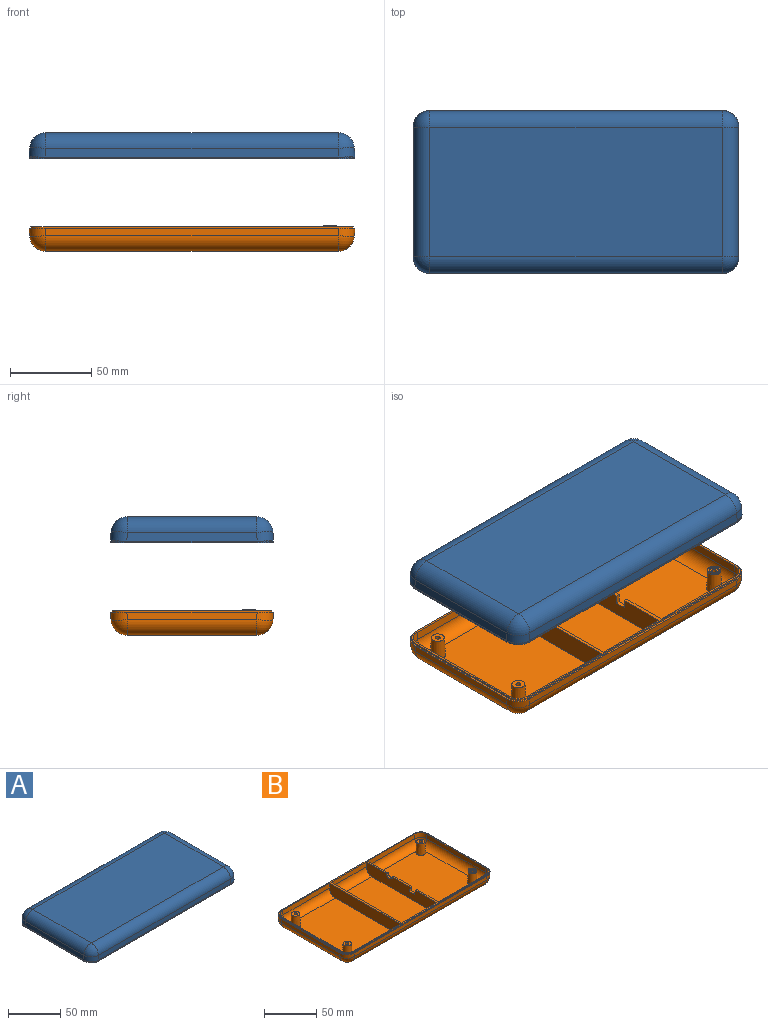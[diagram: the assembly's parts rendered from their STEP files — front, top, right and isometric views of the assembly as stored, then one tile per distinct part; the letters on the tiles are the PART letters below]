
ASSEMBLY  parts=2 mates=1
PART A: 92 faces, bbox 200.3x100.3x16.3 mm
  f0: plane 79.45x46.64mm, normal (0,0,-1), area 3705.3mm2, adj f3,f4,f28,f31
  f1: plane 48x5.42mm, normal (0,1,-0.05), area 258.9mm2, adj f4,f10,f28,f31
  f2: plane 48x5.42mm, normal (0,-1,-0.05), area 258.9mm2, adj f3,f10,f28,f31
  f3: cylinder r=8mm len=47.43mm, axis (-1,0,0), area 571.4mm2, adj f0,f2,f28,f31
  f4: cylinder r=8mm len=47.43mm, axis (-1,0,0), area 571.4mm2, adj f0,f1,f28,f31
  f5: plane 79.45x63.04mm, normal (0,0,-1), area 4871mm2, adj f8,f9,f14,f30,f32,f33
  f6: plane 64.01x5.42mm, normal (0,1,-0.05), area 345.8mm2, adj f9,f10,f22,f30
  f7: plane 64.01x5.42mm, normal (0,-1,-0.05), area 345.8mm2, adj f8,f10,f21,f30
  f8: cylinder r=8mm len=63.44mm, axis (-1,0,0), area 768.2mm2, adj f5,f7,f17,f30
  f9: cylinder r=8mm len=63.44mm, axis (-1,0,0), area 768.2mm2, adj f5,f6,f16,f30
  f10: plane 198.34x98.34mm, normal (0,0,-1), area 957.4mm2, adj f1,f2,f6,f7,f20,f21,f22,f23
  f11: plane 79.45x63.04mm, normal (0,0,-1), area 4871mm2, adj f12,f13,f15,f29,f35,f37
  f12: cylinder r=8mm len=79.45mm, axis (0,1,0), area 965.1mm2, adj f11,f18,f19,f27
  f13: cylinder r=8mm len=63.44mm, axis (-1,0,0), area 768.2mm2, adj f11,f18,f26,f29
  f14: cylinder r=8mm len=79.45mm, axis (0,1,0), area 965.1mm2, adj f5,f16,f17,f25
  f15: cylinder r=8mm len=63.44mm, axis (-1,0,0), area 768.2mm2, adj f11,f19,f24,f29
  f16: sphere r=8mm, area 95.3mm2, adj f9,f14,f22
  f17: sphere r=8mm, area 95.3mm2, adj f8,f14,f21
  f18: sphere r=8mm, area 95.3mm2, adj f12,f13,f20
  f19: sphere r=8mm, area 95.3mm2, adj f12,f15,f23
  f20: cylinder r=8mm len=8.27mm, axis (-0.05,0.05,-1), area 68.2mm2, adj f10,f18,f26,f27
  f21: cylinder r=8mm len=8.27mm, axis (0.05,0.05,-1), area 68.2mm2, adj f7,f10,f17,f25
  f22: cylinder r=8mm len=8.27mm, axis (0.05,-0.05,-1), area 68.2mm2, adj f6,f10,f16,f25
  f23: cylinder r=8mm len=8.27mm, axis (-0.05,-0.05,-1), area 68.2mm2, adj f10,f19,f24,f27
  f24: plane 64.01x5.42mm, normal (0,1,-0.05), area 345.8mm2, adj f10,f15,f23,f29
  f25: plane 80.02x5.42mm, normal (-1,0,-0.05), area 432.6mm2, adj f10,f14,f21,f22
  f26: plane 64.01x5.42mm, normal (0,-1,-0.05), area 345.8mm2, adj f10,f13,f20,f29
  f27: plane 80.02x5.42mm, normal (1,0,-0.05), area 432.6mm2, adj f10,f12,f20,f23
  f28: plane 96.16x13.17mm, normal (1,0,-0.05), area 1216.5mm2, adj f0,f1,f2,f3,f4,f10
  f29: plane 96.16x13.17mm, normal (-1,0,-0.05), area 1216.5mm2, adj f10,f11,f13,f15,f24,f26
  f30: plane 96.16x13.17mm, normal (1,0,-0.05), area 1216.5mm2, adj f5,f6,f7,f8,f9,f10
  f31: plane 96.16x13.17mm, normal (-1,0,-0.05), area 1216.5mm2, adj f0,f1,f2,f3,f4,f10
  f32: cone r=4mm half-angle=3deg, axis (0,0,1), area 329.7mm2, adj f5,f87
  f33: cone r=4mm half-angle=3deg, axis (0,0,1), area 355mm2, adj f5,f34
  f34: plane 8x8mm, normal (0,0,-1), area 47.1mm2, adj f33,f86
  f35: cone r=4mm half-angle=3deg, axis (0,0,1), area 355mm2, adj f11,f36
  f36: plane 8x8mm, normal (0,0,-1), area 47.1mm2, adj f35,f84
  f37: cone r=4mm half-angle=3deg, axis (0,0,1), area 355mm2, adj f11,f38
  f38: plane 8x8mm, normal (0,0,-1), area 47.1mm2, adj f37,f82
  f39: plane 199.99x99.99mm, normal (0,0,-1), area 579.7mm2, adj f40,f41,f42,f43,f44,f45,f46,f47
  f40: plane 180.02x1mm, normal (0,-1,0), area 180mm2, adj f10,f39,f41,f47
  f41: extruded ~8.99x8.99mm, area 14.1mm2, adj f10,f39,f40,f42
  f42: plane 80.02x1mm, normal (1,0,0), area 80mm2, adj f10,f39,f41,f43
  f43: extruded ~8.99x8.99mm, area 14.1mm2, adj f10,f39,f42,f44
  f44: plane 180.02x1mm, normal (0,1,0), area 180mm2, adj f10,f39,f43,f45
  f45: extruded ~8.99x8.99mm, area 14.1mm2, adj f10,f39,f44,f46
  f46: plane 80.02x1mm, normal (-1,0,0), area 80mm2, adj f10,f39,f45,f47
  f47: extruded ~8.99x8.99mm, area 14.1mm2, adj f10,f39,f40,f46
  f48: plane 180.02x1mm, normal (0,1,0), area 180mm2, adj f39,f49,f55,f76
  f49: extruded ~9.99x9.99mm, area 15.7mm2, adj f39,f48,f50,f77
  f50: plane 80.02x1mm, normal (-1,0,0), area 80mm2, adj f39,f49,f51,f78
  f51: extruded ~9.99x9.99mm, area 15.7mm2, adj f39,f50,f52,f79
  f52: plane 180.02x1mm, normal (0,-1,0), area 180mm2, adj f39,f51,f53,f80
  f53: extruded ~9.99x9.99mm, area 15.7mm2, adj f39,f52,f54,f73
  f54: plane 80.02x1mm, normal (1,0,0), area 80mm2, adj f39,f53,f55,f74
  f55: extruded ~9.99x9.99mm, area 15.7mm2, adj f39,f48,f54,f75
  f56: plane 179.45x79.45mm, normal (0,0,1), area 14256.9mm2, adj f57,f59,f61,f63
  f57: cylinder r=10mm len=179.45mm, axis (-1,0,0), area 2724.8mm2, adj f56,f58,f64,f65
  f58: sphere r=10mm, area 148.9mm2, adj f57,f59,f66
  f59: cylinder r=10mm len=79.45mm, axis (0,1,0), area 1206.4mm2, adj f56,f58,f60,f67
  f60: sphere r=10mm, area 148.9mm2, adj f59,f61,f68
  f61: cylinder r=10mm len=179.45mm, axis (-1,0,0), area 2724.8mm2, adj f56,f60,f62,f69
  f62: sphere r=10mm, area 148.9mm2, adj f61,f63,f70
  f63: cylinder r=10mm len=79.45mm, axis (0,1,0), area 1206.4mm2, adj f56,f62,f64,f71
  f64: sphere r=10mm, area 148.9mm2, adj f57,f63,f72
  f65: plane 180.02x5.42mm, normal (0,-1,0.05), area 975.3mm2, adj f57,f66,f72,f80
  f66: cylinder r=10mm len=10.27mm, axis (-0.05,-0.05,-1), area 85.2mm2, adj f58,f65,f67,f79
  f67: plane 80.02x5.42mm, normal (-1,0,0.05), area 432.6mm2, adj f59,f66,f68,f78
  f68: cylinder r=10mm len=10.27mm, axis (-0.05,0.05,-1), area 85.2mm2, adj f60,f67,f69,f77
  f69: plane 180.02x5.42mm, normal (0,1,0.05), area 975.3mm2, adj f61,f68,f70,f76
  f70: cylinder r=10mm len=10.27mm, axis (0.05,0.05,-1), area 85.2mm2, adj f62,f69,f71,f75
  f71: plane 80.02x5.42mm, normal (1,0,0.05), area 432.6mm2, adj f63,f70,f72,f74
  f72: cylinder r=10mm len=10.27mm, axis (0.05,-0.05,-1), area 85.2mm2, adj f64,f65,f71,f73
  f73: bspline ~10.33x10.33mm, area 2.1mm2, adj f53,f72,f74,f80
  f74: cylinder r=2mm len=80.02mm, axis (0,1,0), area 8.4mm2, adj f54,f71,f73,f75
  f75: bspline ~10.33x10.33mm, area 2.1mm2, adj f55,f70,f74,f76
  f76: cylinder r=2mm len=180.02mm, axis (-1,0,0), area 18.9mm2, adj f48,f69,f75,f77
  f77: bspline ~10.33x10.33mm, area 2.1mm2, adj f49,f68,f76,f78
  f78: cylinder r=2mm len=80.02mm, axis (0,1,0), area 8.4mm2, adj f50,f67,f77,f79
  f79: bspline ~10.33x10.33mm, area 2.1mm2, adj f51,f66,f78,f80
  f80: cylinder r=2mm len=180.02mm, axis (-1,0,0), area 18.9mm2, adj f52,f65,f73,f79
  f81: cone r=0mm half-angle=59deg, axis (0,0,-1), area 3.7mm2, adj f82
  f82: cylinder r=1mm len=10mm, axis (0,0,-1), area 62.8mm2, adj f38,f81
  f83: cone r=0mm half-angle=59deg, axis (0,0,-1), area 3.7mm2, adj f84
  f84: cylinder r=1mm len=10mm, axis (0,0,-1), area 62.8mm2, adj f36,f83
  f85: cone r=0mm half-angle=59deg, axis (0,0,-1), area 3.7mm2, adj f86
  f86: cylinder r=1mm len=10mm, axis (0,0,-1), area 62.8mm2, adj f34,f85
  f87: plane 8.11x8.11mm, normal (0,0,-1), area 23.3mm2, adj f32,f88
  f88: cylinder r=3mm len=6mm, axis (0,0,1), area 18.8mm2, adj f87,f91
  f89: cone r=0mm half-angle=59deg, axis (0,0,-1), area 3.7mm2, adj f90
  f90: cylinder r=1mm len=10mm, axis (0,0,-1), area 62.8mm2, adj f89,f91
  f91: plane 6x6mm, normal (0,0,-1), area 25.1mm2, adj f88,f90
PART B: 86 faces, bbox 199.9x99.9x16 mm
  f0: plane 6x6mm, normal (0,0,1), area 21.2mm2, adj f4,f85
  f1: plane 197.99x97.99mm, normal (0,0,1), area 879.8mm2, adj f7,f8,f12,f13,f17,f18,f19,f20
  f2: cylinder r=1.5mm len=5mm, axis (0,0,1), area 47.1mm2, adj f39,f78
  f3: cylinder r=1.5mm len=5mm, axis (0,0,1), area 47.1mm2, adj f43,f76
  f4: cylinder r=1.5mm len=5mm, axis (0,0,1), area 47.1mm2, adj f0,f74
  f5: cylinder r=1.5mm len=5mm, axis (0,0,1), area 47.1mm2, adj f41,f72
  f6: plane 79.45x63.04mm, normal (0,0,1), area 4871mm2, adj f9,f10,f28,f37,f42,f44
  f7: plane 64.01x5.42mm, normal (0,-1,0.05), area 345.8mm2, adj f1,f10,f22,f37
  f8: plane 64.01x5.42mm, normal (0,1,0.05), area 345.8mm2, adj f1,f9,f21,f37
  f9: cylinder r=8mm len=63.44mm, axis (1,0,0), area 767.6mm2, adj f6,f8,f26,f37
  f10: cylinder r=8mm len=63.44mm, axis (1,0,0), area 767.6mm2, adj f6,f7,f30,f37
  f11: plane 79.45x63.04mm, normal (0,0,1), area 4871mm2, adj f14,f15,f29,f34,f38,f40
  f12: plane 64.01x5.42mm, normal (0,-1,0.05), area 345.8mm2, adj f1,f15,f23,f34
  f13: plane 64.01x5.42mm, normal (0,1,0.05), area 345.8mm2, adj f1,f14,f24,f34
  f14: cylinder r=8mm len=63.44mm, axis (1,0,0), area 767.6mm2, adj f11,f13,f27,f34
  f15: cylinder r=8mm len=63.44mm, axis (1,0,0), area 767.6mm2, adj f11,f12,f31,f34
  f16: plane 79.45x46.64mm, normal (0,0,1), area 3705.3mm2, adj f25,f32,f35,f36
  f17: plane 80.02x5.42mm, normal (1,0,0.05), area 432.6mm2, adj f1,f23,f24,f29
  f18: plane 48x5.42mm, normal (0,-1,0.05), area 258.9mm2, adj f1,f32,f35,f36
  f19: plane 80.02x5.42mm, normal (-1,0,0.05), area 432.6mm2, adj f1,f21,f22,f28
  f20: plane 48x5.42mm, normal (0,1,0.05), area 258.9mm2, adj f1,f25,f35,f36
  f21: cylinder r=8mm len=8.28mm, axis (-0.05,0.05,-1), area 69.6mm2, adj f1,f8,f19,f26
  f22: cylinder r=8mm len=8.28mm, axis (-0.05,-0.05,-1), area 69.6mm2, adj f1,f7,f19,f30
  f23: cylinder r=8mm len=8.28mm, axis (0.05,-0.05,-1), area 69.6mm2, adj f1,f12,f17,f31
  f24: cylinder r=8mm len=8.28mm, axis (0.05,0.05,-1), area 69.6mm2, adj f1,f13,f17,f27
  f25: cylinder r=8mm len=47.43mm, axis (1,0,0), area 570mm2, adj f16,f20,f35,f36
  f26: sphere r=8mm, area 93.8mm2, adj f9,f21,f28
  f27: sphere r=8mm, area 93.8mm2, adj f14,f24,f29
  f28: cylinder r=8mm len=79.45mm, axis (0,-1,0), area 965.1mm2, adj f6,f19,f26,f30
  f29: cylinder r=8mm len=79.45mm, axis (0,-1,0), area 965.1mm2, adj f11,f17,f27,f31
  f30: sphere r=8mm, area 93.8mm2, adj f10,f22,f28
  f31: sphere r=8mm, area 93.8mm2, adj f15,f23,f29
  f32: cylinder r=8mm len=47.43mm, axis (1,0,0), area 570mm2, adj f16,f18,f35,f36
  f33: plane 24.11x2mm, normal (0,0,1), area 48.2mm2, adj f36,f37,f79,f82
  f34: plane 95.99x13mm, normal (-1,0,0.05), area 1216.5mm2, adj f1,f11,f12,f13,f14,f15
  f35: plane 95.99x13mm, normal (1,0,0.05), area 1216.5mm2, adj f1,f16,f18,f20,f25,f32
  f36: plane 95.99x13mm, normal (-1,0,0.05), area 1157.7mm2, adj f1,f16,f18,f20,f25,f32,f33,f79
  f37: plane 95.99x13mm, normal (1,0,0.05), area 1155.9mm2, adj f1,f6,f7,f8,f9,f10,f33,f79
  f38: cone r=4mm half-angle=3deg, axis (0,0,-1), area 355mm2, adj f11,f39
  f39: plane 8x8mm, normal (0,0,1), area 43.2mm2, adj f2,f38
  f40: cone r=4mm half-angle=3deg, axis (0,0,-1), area 355mm2, adj f11,f41
  f41: plane 8x8mm, normal (0,0,1), area 43.2mm2, adj f5,f40
  f42: cone r=4mm half-angle=3deg, axis (0,0,-1), area 355mm2, adj f6,f43
  f43: plane 8x8mm, normal (0,0,1), area 43.2mm2, adj f3,f42
  f44: cone r=4mm half-angle=3deg, axis (0,0,-1), area 355mm2, adj f6,f84
  f45: plane 199.9x99.9mm, normal (0,0,1), area 550mm2, adj f46,f47,f48,f49,f50,f51,f52,f53
  f46: extruded ~8.99x8.99mm, area 14.1mm2, adj f1,f45,f47,f53
  f47: plane 80.02x1mm, normal (-1,0,0), area 80mm2, adj f1,f45,f46,f48
  f48: extruded ~8.99x8.99mm, area 14.1mm2, adj f1,f45,f47,f49
  f49: plane 180.02x1mm, normal (0,-1,0), area 180mm2, adj f1,f45,f48,f50
  f50: extruded ~8.99x8.99mm, area 14.1mm2, adj f1,f45,f49,f51
  f51: plane 80.02x1mm, normal (1,0,0), area 80mm2, adj f1,f45,f50,f52
  f52: extruded ~8.99x8.99mm, area 14.1mm2, adj f1,f45,f51,f53
  f53: plane 180.02x1mm, normal (0,1,0), area 180mm2, adj f1,f45,f46,f52
  f54: plane 179.45x79.45mm, normal (0,0,-1), area 14143.8mm2, adj f55,f58,f59,f62,f71,f73,f75,f77
  f55: cylinder r=10mm len=179.45mm, axis (1,0,0), area 2724.8mm2, adj f54,f56,f57,f70
  f56: sphere r=10mm, area 146.6mm2, adj f55,f58,f69
  f57: sphere r=10mm, area 146.6mm2, adj f55,f59,f68
  f58: cylinder r=10mm len=79.45mm, axis (0,-1,0), area 1206.4mm2, adj f54,f56,f60,f67
  f59: cylinder r=10mm len=79.45mm, axis (0,-1,0), area 1206.4mm2, adj f54,f57,f61,f66
  f60: sphere r=10mm, area 146.6mm2, adj f58,f62,f65
  f61: sphere r=10mm, area 146.6mm2, adj f59,f62,f64
  f62: cylinder r=10mm len=179.45mm, axis (1,0,0), area 2724.8mm2, adj f54,f60,f61,f63
  f63: plane 179.92x4.52mm, normal (0,1,-0.05), area 813.9mm2, adj f45,f62,f64,f65
  f64: cylinder r=10mm len=10.23mm, axis (0.05,-0.05,-1), area 73.4mm2, adj f45,f61,f63,f66
  f65: cylinder r=10mm len=10.23mm, axis (-0.05,-0.05,-1), area 73.4mm2, adj f45,f60,f63,f67
  f66: plane 79.92x4.52mm, normal (-1,0,-0.05), area 360.9mm2, adj f45,f59,f64,f68
  f67: plane 79.92x4.52mm, normal (1,0,-0.05), area 360.9mm2, adj f45,f58,f65,f69
  f68: cylinder r=10mm len=10.23mm, axis (0.05,0.05,-1), area 73.4mm2, adj f45,f57,f66,f70
  f69: cylinder r=10mm len=10.23mm, axis (-0.05,0.05,-1), area 73.4mm2, adj f45,f56,f67,f70
  f70: plane 179.92x4.52mm, normal (0,-1,-0.05), area 813.9mm2, adj f45,f55,f68,f69
  f71: cylinder r=3mm len=10mm, axis (0,0,1), area 188.5mm2, adj f54,f72
  f72: plane 6x6mm, normal (0,0,-1), area 21.2mm2, adj f5,f71
  f73: cylinder r=3mm len=10mm, axis (0,0,1), area 188.5mm2, adj f54,f74
  f74: plane 6x6mm, normal (0,0,-1), area 21.2mm2, adj f4,f73
  f75: cylinder r=3mm len=10mm, axis (0,0,1), area 188.5mm2, adj f54,f76
  f76: plane 6x6mm, normal (0,0,-1), area 21.2mm2, adj f3,f75
  f77: cylinder r=3mm len=10mm, axis (0,0,1), area 188.5mm2, adj f54,f78
  f78: plane 6x6mm, normal (0,0,-1), area 21.2mm2, adj f2,f77
  f79: plane 5.3x2.55mm, normal (0,-1,0), area 11.9mm2, adj f33,f36,f37,f81
  f80: plane 5.3x2.55mm, normal (0,1,0), area 11.9mm2, adj f1,f36,f37,f81
  f81: plane 6.81x2.55mm, normal (0.05,0,1), area 17.4mm2, adj f36,f37,f79,f80
  f82: cylinder r=3.94mm len=7.87mm, axis (1,0,-0.05), area 27.7mm2, adj f1,f33,f36,f37
  f83: plane 8x8mm, normal (0,0,1), area 22mm2, adj f84,f85
  f84: cylinder r=4mm len=8mm, axis (0,0,1), area 25.1mm2, adj f44,f83
  f85: cylinder r=3mm len=6mm, axis (0,0,1), area 18.8mm2, adj f0,f83
PLACE A t=(-22.03,-10.73,60.77)mm
PLACE B t=(-22.03,-10.73,18.07)mm fixed
MATE slider A.f37 <-> B.f5  axis (0,0,-1) through (-107.03,-45.73,60.77)mm
